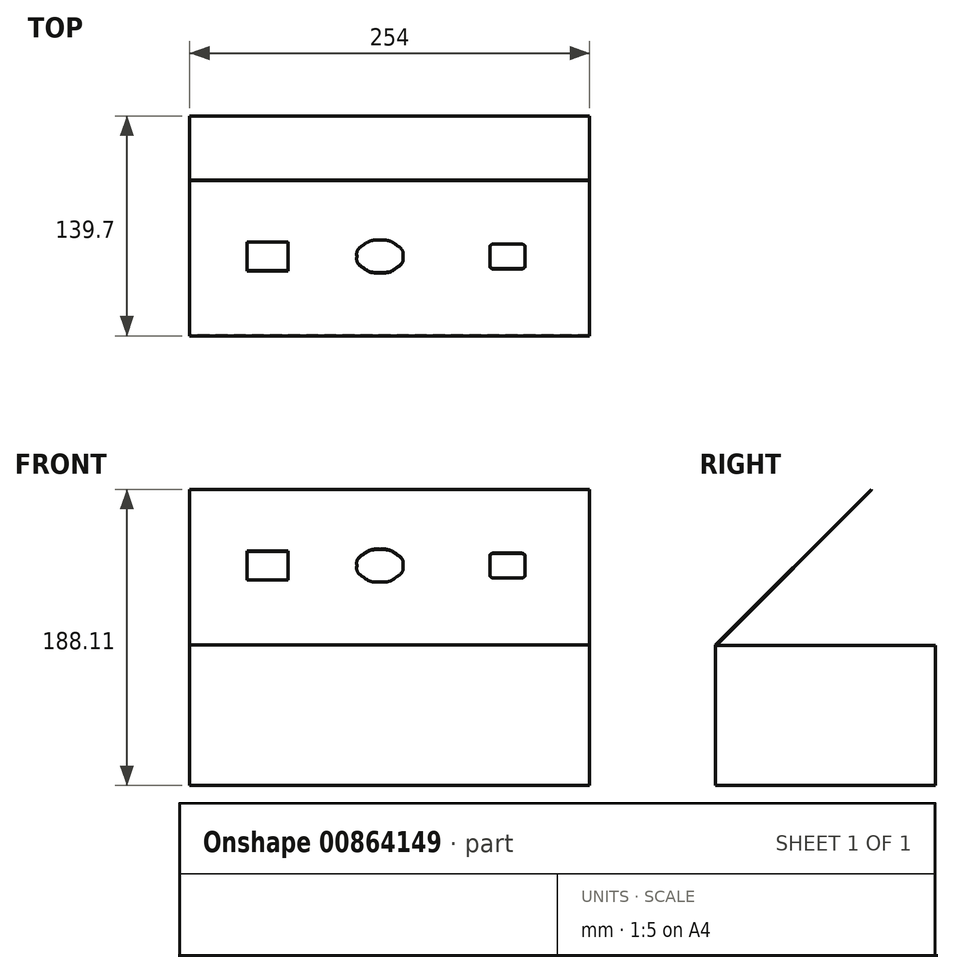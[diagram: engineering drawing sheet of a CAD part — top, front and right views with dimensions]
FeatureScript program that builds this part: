
annotation { "Feature Type Name" : "Feature", "Feature Type Description" : "" }
export const myFeature = defineFeature(function(context is Context, id is Id, definition is map)
    precondition{}
    {
        {
            var Q0;
            Q0=qCreatedBy(makeId("Right.planeOp"),FACE);
            var sketch = newSketch(context, id + "F0", { "sketchPlane" : qUnion([Q0])});
            skLineSegment(sketch, "E0.bottom", {"start": v(0, 0) * mm, "end": v(-139.7, 0) * mm});
            skLineSegment(sketch, "E0.top", {"start": v(0, 88.9) * mm, "end": v(-139.3, 88.9) * mm});
            skLineSegment(sketch, "E0.left", {"start": v(0, 0) * mm, "end": v(0, 88.9) * mm});
            skLineSegment(sketch, "E0.right", {"start": v(-139.7, 0) * mm, "end": v(-139.7, 89.32) * mm});
            skLineSegment(sketch, "E1", {"start": v(-139.7, 89.32) * mm, "end": v(-40.92, 188.1) * mm});
            skLineSegment(sketch, "E2", {"start": v(-40.92, 188.1) * mm, "end": v(-40.63, 187.82) * mm});
            skLineSegment(sketch, "E3", {"start": v(-40.63, 187.82) * mm, "end": v(-139.3, 89.15) * mm});
            skLineSegment(sketch, "E4", {"start": v(-139.3, 88.9) * mm, "end": v(-139.3, 89.15) * mm});
            skLineSegment(sketch, "E5", {"start": v(-139.3, 88.9) * mm, "end": v(-139.7, 88.9) * mm, "construction": true});
            skSolve(sketch);
        }
        {
            var Q0;
            Q0=qSketchRegion(id+"F0",true);
            extrude(context, id + "F1", {"entities" : qUnion([Q0]), "endBound" : BoundingType.SYMMETRIC, "depth" : 254 * mm, "offsetDistance" : 25.4 * mm});
        }
        {
            var Q0;
            Q0=makeQuery(id+"F1.opExtrude","SWEPT_FACE",FACE,{"disambiguationData":[OSD([sQuery(id+"F0.wireOp",EDGE,"E1")])]});
            var sketch = newSketch(context, id + "F2", { "sketchPlane" : qUnion([Q0])});
            skLineSegment(sketch, "E6", {"start": v(-64.58, 22.57) * mm, "end": v(-64.58, 48.76) * mm});
            skLineSegment(sketch, "E7", {"start": v(-64.58, 48.76) * mm, "end": v(-90.78, 48.76) * mm});
            skLineSegment(sketch, "E8", {"start": v(-90.78, 48.76) * mm, "end": v(-90.78, 22.57) * mm});
            skLineSegment(sketch, "E9", {"start": v(-90.78, 22.57) * mm, "end": v(-64.58, 22.57) * mm});
            skLineSegment(sketch, "E10", {"start": v(63.6, 44.4) * mm, "end": v(63.6, 26.93) * mm});
            skLineSegment(sketch, "E11", {"start": v(83.45, 46.78) * mm, "end": v(65.99, 46.78) * mm});
            skLineSegment(sketch, "E12", {"start": v(65.99, 24.55) * mm, "end": v(83.45, 24.55) * mm});
            skLineSegment(sketch, "E13", {"start": v(85.83, 26.93) * mm, "end": v(85.83, 44.4) * mm});
            skLineSegment(sketch, "E14", {"start": v(-128.48, 104.72) * mm, "end": v(125.52, 104.72) * mm, "construction": true});
            skLineSegment(sketch, "E15", {"start": v(-128.48, -34.19) * mm, "end": v(-128.48, 104.72) * mm, "construction": true});
            skLineSegment(sketch, "E16", {"start": v(125.52, -34.19) * mm, "end": v(125.52, 104.72) * mm, "construction": true});
            skLineSegment(sketch, "E17", {"start": v(125.52, -34.19) * mm, "end": v(-128.48, -34.19) * mm, "construction": true});
            skFitSpline(sketch, "E18", {"points": [v(63.6, 26.93) * mm, v(63.6, 26.31) * mm, v(63.87, 25.7) * mm, v(64.3, 25.25) * mm]});
            skFitSpline(sketch, "E19", {"points": [v(64.3, 25.25) * mm, v(64.75, 24.8) * mm, v(65.37, 24.55) * mm, v(65.99, 24.55) * mm]});
            skFitSpline(sketch, "E20", {"points": [v(65.99, 46.78) * mm, v(65.37, 46.78) * mm, v(64.75, 46.52) * mm, v(64.3, 46.08) * mm]});
            skFitSpline(sketch, "E21", {"points": [v(64.3, 46.08) * mm, v(63.87, 45.64) * mm, v(63.6, 45.02) * mm, v(63.6, 44.4) * mm]});
            skFitSpline(sketch, "E22", {"points": [v(85.83, 44.4) * mm, v(85.83, 45.02) * mm, v(85.58, 45.64) * mm, v(85.14, 46.08) * mm]});
            skFitSpline(sketch, "E23", {"points": [v(85.14, 46.08) * mm, v(84.7, 46.52) * mm, v(84.08, 46.78) * mm, v(83.45, 46.78) * mm]});
            skFitSpline(sketch, "E24", {"points": [v(83.45, 24.55) * mm, v(84.08, 24.55) * mm, v(84.7, 24.8) * mm, v(85.14, 25.25) * mm]});
            skFitSpline(sketch, "E25", {"points": [v(85.14, 25.25) * mm, v(85.58, 25.7) * mm, v(85.83, 26.31) * mm, v(85.83, 26.93) * mm]});
            skFitSpline(sketch, "E26", {"points": [v(-6.24, 50.35) * mm, v(-10.09, 50.35) * mm, v(-13.9, 48.77) * mm, v(-16.62, 46.05) * mm]});
            skFitSpline(sketch, "E27", {"points": [v(-16.62, 46.05) * mm, v(-19.34, 43.33) * mm, v(-20.93, 39.5) * mm, v(-20.93, 35.66) * mm, v(-20.93, 31.82) * mm, v(-19.34, 28) * mm, v(-16.62, 25.28) * mm]});
            skFitSpline(sketch, "E28", {"points": [v(-16.62, 25.28) * mm, v(-13.9, 22.56) * mm, v(-10.09, 20.98) * mm, v(-6.24, 20.98) * mm, v(-2.4, 20.98) * mm, v(1.42, 22.56) * mm, v(4.14, 25.28) * mm]});
            skFitSpline(sketch, "E29", {"points": [v(4.14, 25.28) * mm, v(6.86, 28) * mm, v(8.44, 31.82) * mm, v(8.44, 35.66) * mm, v(8.44, 39.5) * mm, v(6.86, 43.33) * mm, v(4.14, 46.05) * mm]});
            skFitSpline(sketch, "E30", {"points": [v(4.14, 46.05) * mm, v(1.42, 48.77) * mm, v(-2.4, 50.35) * mm, v(-6.24, 50.35) * mm]});
            skSolve(sketch);
        }
        {
            var Q0;
            Q0=qSketchRegion(id+"F2",true);
            var Q1;
            Q1=makeQuery(id+"F1.opExtrude","SWEPT_FACE",FACE,{"disambiguationData":[OSD([sQuery(id+"F0.wireOp",EDGE,"E3")])]});
            extrude(context, id + "F3", {"entities" : qUnion([Q0]), "operationType" : NewBodyOperationType.REMOVE, "endBound" : BoundingType.UP_TO_SURFACE, "oppositeDirection" : true, "depth" : 25.4 * mm, "endBoundEntityFace" : qUnion([Q1]), "offsetDistance" : 25.4 * mm});
        }
    });
